# Revit family: In Between Table SK15
name_source: partatom
category: Furniture
revit_build: Autodesk Revit 2017 (Build: 20171027_0315(x64)
units: mm (PartAtom-declared; Revit-internal decimal feet)

## family parameters
Always vertical = Yes
Cut with Voids When Loaded = No
OmniClass Number = 23.40.20.00
OmniClass Title = General Furniture and Specialties
Room Calculation Point = No
Shared = No
Work Plane-Based = No

## types (1)
- In Between Table SK15
    Base = &tradition White Oak Oiled Vertical
    Description = Sitting within the larger In Between series, this lounge 
table carefully echoes many aspects of the In Between chair, 
from its gentle curvature to the outward splay of its legs. 
It is available in two heights and comes in three finishes: 
black lacquered oak; white oiled oak; and smoked oiled oak.
    Design = Sami Kallio
    Design Year = 2014
    Diameter = 90cm /  35.4in
    Height = 48cm / 18.9in
    Manufacturer = &tradition
    Model = In Between Table SK15
    Packaging Dimensions = H: 7cm/2.8in W: 105cm/41.3in D: 105 cm/41.3in
    Table Top = &tradition White Oak Oiled Horizontal
    Type Comments = In Between series
    URL = https://www.andtradition.com
    Variation 1 = Oiled Smoked Oak
    Variation 2 = Lacquered Black Oak
    Weight = 13 kg

## geometry (parser evidence)
native form markers: Sweep x2
no freeform markers — native parametric forms only
